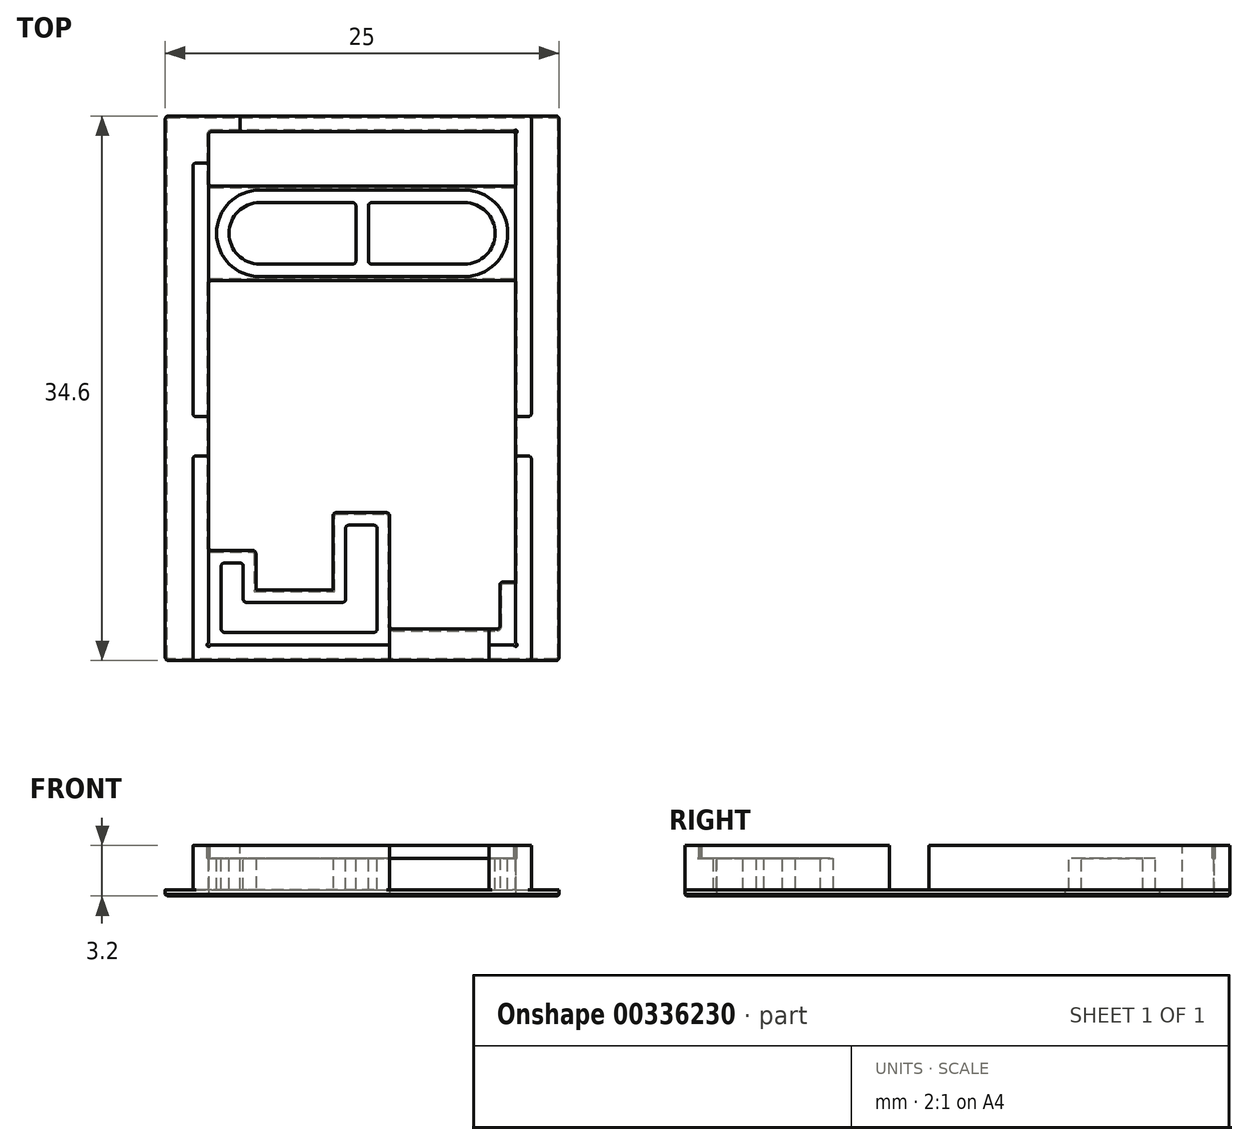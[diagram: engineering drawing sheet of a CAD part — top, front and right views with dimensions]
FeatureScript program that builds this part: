
annotation { "Feature Type Name" : "Feature", "Feature Type Description" : "" }
export const myFeature = defineFeature(function(context is Context, id is Id, definition is map)
    precondition{}
    {
        {
            var Q0;
            Q0=qCreatedBy(makeId("Front.planeOp"),FACE);
            var sketch = newSketch(context, id + "F0", { "sketchPlane" : qUnion([Q0])});
            skLineSegment(sketch, "E0", {"start": v(0, 0) * mm, "end": v(0, 2) * mm});
            skLineSegment(sketch, "E1", {"start": v(0, 0) * mm, "end": v(0, -0.4) * mm});
            skLineSegment(sketch, "E2", {"start": v(0, 2) * mm, "end": v(0, 2.8) * mm});
            skSolve(sketch);
        }
        {
            var Q0;
            Q0=qCreatedBy(makeId("Top.planeOp"),FACE);
            var sketch = newSketch(context, id + "F1", { "sketchPlane" : qUnion([Q0])});
            skLineSegment(sketch, "E3.bottom", {"start": v(9.75, 16.3) * mm, "end": v(-9.75, 16.3) * mm, "construction": true});
            skLineSegment(sketch, "E3.top", {"start": v(9.75, -16.3) * mm, "end": v(-9.75, -16.3) * mm, "construction": true});
            skLineSegment(sketch, "E3.left", {"start": v(9.75, 16.3) * mm, "end": v(9.75, -16.3) * mm, "construction": true});
            skLineSegment(sketch, "E3.right", {"start": v(-9.75, 16.3) * mm, "end": v(-9.75, -16.3) * mm, "construction": true});
            skPoint(sketch, "E3.middle", {"position": v(0, 0) * mm});
            skLineSegment(sketch, "E4", {"start": v(-9.75, 6.3) * mm, "end": v(9.75, 6.3) * mm, "construction": true});
            skLineSegment(sketch, "E5", {"start": v(1.75, -16.3) * mm, "end": v(1.75, -7.9) * mm, "construction": true});
            skLineSegment(sketch, "E6", {"start": v(-1.85, -16.3) * mm, "end": v(-1.85, -7.9) * mm, "construction": true});
            skLineSegment(sketch, "E7", {"start": v(-1.85, -7.9) * mm, "end": v(1.75, -7.9) * mm, "construction": true});
            skLineSegment(sketch, "E8", {"start": v(8.75, -16.3) * mm, "end": v(8.75, -12.3) * mm, "construction": true});
            skLineSegment(sketch, "E9", {"start": v(8.75, -12.3) * mm, "end": v(9.75, -12.3) * mm, "construction": true});
            skLineSegment(sketch, "E10", {"start": v(-9.75, 6.84) * mm, "end": v(9.75, 6.84) * mm, "construction": true});
            skLineSegment(sketch, "E11", {"start": v(-9.75, 12.84) * mm, "end": v(9.75, 12.84) * mm, "construction": true});
            skLineSegment(sketch, "E12", {"start": v(-1.85, -12.8) * mm, "end": v(-9.75, -12.8) * mm, "construction": true});
            skLineSegment(sketch, "E13", {"start": v(-9.75, -10.3) * mm, "end": v(-6.75, -10.3) * mm, "construction": true});
            skLineSegment(sketch, "E14", {"start": v(-6.75, -10.3) * mm, "end": v(-6.75, -12.8) * mm, "construction": true});
            skSolve(sketch);
        }
        {
            var Q0;
            Q0=qCreatedBy(makeId("Top.planeOp"),FACE);
            var sketch = newSketch(context, id + "F2", { "sketchPlane" : qUnion([Q0])});
            skLineSegment(sketch, "E15.bottom", {"start": v(12.5, 17.3) * mm, "end": v(-12.5, 17.3) * mm});
            skLineSegment(sketch, "E15.top", {"start": v(12.5, -17.3) * mm, "end": v(8.75, -17.3) * mm});
            skLineSegment(sketch, "E15.left", {"start": v(12.5, 17.3) * mm, "end": v(12.5, -17.3) * mm});
            skLineSegment(sketch, "E15.right", {"start": v(-12.5, 17.3) * mm, "end": v(-12.5, -17.3) * mm});
            skPoint(sketch, "E15.middle", {"position": v(0, 0) * mm});
            skLineSegment(sketch, "E16.0", {"start": v(9.75, 16.3) * mm, "end": v(-9.75, 16.3) * mm});
            skLineSegment(sketch, "E17.0", {"start": v(-9.75, 12.84) * mm, "end": v(9.75, 12.84) * mm});
            skLineSegment(sketch, "E18", {"start": v(-9.75, 16.3) * mm, "end": v(-9.75, 12.84) * mm});
            skLineSegment(sketch, "E19", {"start": v(9.75, 16.3) * mm, "end": v(9.75, 12.84) * mm});
            skLineSegment(sketch, "E20.0", {"start": v(-9.75, 6.84) * mm, "end": v(9.75, 6.84) * mm});
            skLineSegment(sketch, "E21.0", {"start": v(-9.75, -10.3) * mm, "end": v(-6.75, -10.3) * mm});
            skLineSegment(sketch, "E22.0", {"start": v(-6.75, -10.3) * mm, "end": v(-6.75, -12.8) * mm});
            skLineSegment(sketch, "E23.0", {"start": v(-1.85, -7.9) * mm, "end": v(1.75, -7.9) * mm});
            skLineSegment(sketch, "E24.0", {"start": v(1.75, -16.3) * mm, "end": v(1.75, -7.9) * mm});
            skLineSegment(sketch, "E25.0", {"start": v(8.75, -16.3) * mm, "end": v(8.75, -12.3) * mm});
            skLineSegment(sketch, "E26.0", {"start": v(8.75, -12.3) * mm, "end": v(9.75, -12.3) * mm});
            skLineSegment(sketch, "E27", {"start": v(9.75, 6.84) * mm, "end": v(9.75, -12.3) * mm});
            skLineSegment(sketch, "E28", {"start": v(1.75, -16.3) * mm, "end": v(1.75, -17.3) * mm});
            skLineSegment(sketch, "E29", {"start": v(8.75, -16.3) * mm, "end": v(8.75, -17.3) * mm});
            skLineSegment(sketch, "E30", {"start": v(-6.75, -12.8) * mm, "end": v(-1.85, -12.8) * mm});
            skLineSegment(sketch, "E31", {"start": v(-1.85, -12.8) * mm, "end": v(-1.85, -7.9) * mm});
            skLineSegment(sketch, "E32", {"start": v(-9.75, 6.84) * mm, "end": v(-9.75, -10.3) * mm});
            skLineSegment(sketch, "E33", {"start": v(1.75, -17.3) * mm, "end": v(-12.5, -17.3) * mm});
            skLineSegment(sketch, "E34", {"start": v(8.75, -17.3) * mm, "end": v(1.75, -17.3) * mm});
            skLineSegment(sketch, "E35", {"start": v(1.75, -15.3) * mm, "end": v(8.75, -15.3) * mm});
            skSolve(sketch);
        }
        {
            var Q0;
            Q0 = qSketchRegion(id + "F2", true);
            var Q1;
            Q1=sQuery(id+"F0.wireOp",EDGE,"E1");
            sweep(context, id + "F3", {"profiles" : qUnion([Q0]), "path" : qUnion([Q1])});
        }
        {
            var Q0;
            Q0=makeQuery(id+"F3.opSweep","CAP_FACE",FACE,{"disambiguationData":[OSD([sQuery(id+"F0.wireOp",VERTEX,"E1.start"),sQuery(id+"F2.wireOp",EDGE,"E15.bottom"),sQuery(id+"F2.wireOp",EDGE,"E15.top"),sQuery(id+"F2.wireOp",EDGE,"E15.left"),sQuery(id+"F2.wireOp",EDGE,"E15.right"),sQuery(id+"F2.wireOp",EDGE,"E16.0"),sQuery(id+"F2.wireOp",EDGE,"E17.0"),sQuery(id+"F2.wireOp",EDGE,"E18"),sQuery(id+"F2.wireOp",EDGE,"E19"),sQuery(id+"F2.wireOp",EDGE,"E20.0"),sQuery(id+"F2.wireOp",EDGE,"E21.0"),sQuery(id+"F2.wireOp",EDGE,"E22.0"),sQuery(id+"F2.wireOp",EDGE,"E23.0"),sQuery(id+"F2.wireOp",EDGE,"E24.0"),sQuery(id+"F2.wireOp",EDGE,"E25.0"),sQuery(id+"F2.wireOp",EDGE,"E26.0"),sQuery(id+"F2.wireOp",EDGE,"E27"),sQuery(id+"F2.wireOp",EDGE,"E28"),sQuery(id+"F2.wireOp",EDGE,"E29"),sQuery(id+"F2.wireOp",EDGE,"E30"),sQuery(id+"F2.wireOp",EDGE,"E31"),sQuery(id+"F2.wireOp",EDGE,"E32"),sQuery(id+"F2.wireOp",EDGE,"E33")])],"isStart":true});
            var sketch = newSketch(context, id + "F4", { "sketchPlane" : qUnion([Q0])});
            skPoint(sketch, "E36.0", {"position": v(9.75, -16.3) * mm});
            skLineSegment(sketch, "E37.bottom", {"start": v(8.75, -12.3) * mm, "end": v(9.75, -12.3) * mm});
            skLineSegment(sketch, "E37.top", {"start": v(8.75, -16.3) * mm, "end": v(9.75, -16.3) * mm});
            skLineSegment(sketch, "E37.left", {"start": v(8.75, -12.3) * mm, "end": v(8.75, -15.3) * mm});
            skLineSegment(sketch, "E37.right", {"start": v(9.75, -12.3) * mm, "end": v(9.75, -16.3) * mm});
            skLineSegment(sketch, "E38.0", {"start": v(9.75, -16.3) * mm, "end": v(-9.75, -16.3) * mm, "construction": true});
            skLineSegment(sketch, "E39", {"start": v(1.75, -7.9) * mm, "end": v(1.75, -16.3) * mm});
            skLineSegment(sketch, "E40", {"start": v(1.75, -16.3) * mm, "end": v(-9.75, -16.3) * mm});
            skLineSegment(sketch, "E41", {"start": v(-9.75, -16.3) * mm, "end": v(-9.75, -10.3) * mm});
            skLineSegment(sketch, "E42", {"start": v(-9.75, -10.3) * mm, "end": v(-6.75, -10.3) * mm});
            skLineSegment(sketch, "E43", {"start": v(-6.75, -10.3) * mm, "end": v(-6.75, -12.8) * mm});
            skLineSegment(sketch, "E44", {"start": v(-6.75, -12.8) * mm, "end": v(-1.85, -12.8) * mm});
            skLineSegment(sketch, "E45", {"start": v(-1.85, -12.8) * mm, "end": v(-1.85, -7.9) * mm});
            skLineSegment(sketch, "E46", {"start": v(-1.85, -7.9) * mm, "end": v(1.75, -7.9) * mm});
            skLineSegment(sketch, "E47", {"start": v(0, 12.84) * mm, "end": v(0, 6.84) * mm, "construction": true});
            skLineSegment(sketch, "E48", {"start": v(-6.5, 9.84) * mm, "end": v(6.5, 9.84) * mm, "construction": true});
            skPoint(sketch, "E49", {"position": v(0, 9.84) * mm});
            skArc(sketch, "E50.0.startCap", {"start": v(-6.5, 7.09) * mm, "mid": v(-9.25, 9.84) * mm, "end": v(-6.5, 12.59) * mm});
            skArc(sketch, "E50.0.endCap", {"start": v(6.5, 12.6) * mm, "mid": v(9.25, 9.84) * mm, "end": v(6.5, 7.09) * mm});
            skLineSegment(sketch, "E50.0.left", {"start": v(-6.5, 12.59) * mm, "end": v(6.5, 12.59) * mm});
            skLineSegment(sketch, "E50.0.right", {"start": v(-6.5, 7.09) * mm, "end": v(6.5, 7.1) * mm});
            skArc(sketch, "E51.0", {"start": v(-6.5, 7.89) * mm, "mid": v(-8.45, 9.84) * mm, "end": v(-6.5, 11.79) * mm});
            skLineSegment(sketch, "E51.1", {"start": v(-6.5, 7.89) * mm, "end": v(6.5, 7.89) * mm});
            skArc(sketch, "E51.2", {"start": v(6.5, 11.8) * mm, "mid": v(8.45, 9.84) * mm, "end": v(6.5, 7.89) * mm});
            skLineSegment(sketch, "E51.3", {"start": v(-6.5, 11.79) * mm, "end": v(-0.4, 11.79) * mm});
            skLineSegment(sketch, "E52.0", {"start": v(-8.95, -15.5) * mm, "end": v(-8.95, -11.1) * mm});
            skLineSegment(sketch, "E52.1", {"start": v(0.95, -15.5) * mm, "end": v(-8.95, -15.5) * mm});
            skLineSegment(sketch, "E52.2", {"start": v(-8.95, -11.1) * mm, "end": v(-7.55, -11.1) * mm});
            skLineSegment(sketch, "E52.3", {"start": v(0.95, -8.7) * mm, "end": v(0.95, -15.5) * mm});
            skLineSegment(sketch, "E52.4", {"start": v(-7.55, -11.1) * mm, "end": v(-7.55, -13.6) * mm});
            skLineSegment(sketch, "E52.5", {"start": v(-7.55, -13.6) * mm, "end": v(-1.05, -13.6) * mm});
            skLineSegment(sketch, "E52.6", {"start": v(-1.05, -13.6) * mm, "end": v(-1.05, -8.7) * mm});
            skLineSegment(sketch, "E52.7", {"start": v(-1.05, -8.7) * mm, "end": v(0.95, -8.7) * mm});
            skLineSegment(sketch, "E53", {"start": v(-0.4, 11.79) * mm, "end": v(-0.4, 7.9) * mm});
            skLineSegment(sketch, "E54", {"start": v(0.4, 11.79) * mm, "end": v(0.4, 7.9) * mm});
            skLineSegment(sketch, "E55", {"start": v(-0.4, 11.79) * mm, "end": v(0.4, 11.79) * mm, "construction": true});
            skLineSegment(sketch, "E56", {"start": v(-0.4, 11.79) * mm, "end": v(-0.4, 11.79) * mm});
            skLineSegment(sketch, "E57", {"start": v(0.4, 11.79) * mm, "end": v(6.5, 11.8) * mm});
            skLineSegment(sketch, "E58", {"start": v(8.75, -16.3) * mm, "end": v(8.05, -16.3) * mm});
            skLineSegment(sketch, "E59", {"start": v(8.05, -16.3) * mm, "end": v(8.05, -15.3) * mm});
            skLineSegment(sketch, "E60", {"start": v(8.05, -15.3) * mm, "end": v(8.75, -15.3) * mm});
            skLineSegment(sketch, "E61", {"start": v(8.75, -15.3) * mm, "end": v(8.75, -16.3) * mm, "construction": true});
            skSolve(sketch);
        }
        {
            var Q0;
            Q0 = qSketchRegion(id + "F4", true);
            var Q1;
            Q1=sQuery(id+"F0.wireOp",EDGE,"E0");
            sweep(context, id + "F5", {"operationType" : NewBodyOperationType.ADD, "profiles" : qUnion([Q0]), "path" : qUnion([Q1])});
        }
        {
            var Q0;
            Q0=qCreatedBy(makeId("Top.planeOp"),FACE);
            var sketch = newSketch(context, id + "F6", { "sketchPlane" : qUnion([Q0])});
            skLineSegment(sketch, "E62.0", {"start": v(8.05, -16.3) * mm, "end": v(9.75, -16.3) * mm});
            skLineSegment(sketch, "E63", {"start": v(8.75, -17.3) * mm, "end": v(10.75, -17.3) * mm});
            skLineSegment(sketch, "E64.0", {"start": v(9.75, 16.3) * mm, "end": v(-9.75, 16.3) * mm, "construction": true});
            skLineSegment(sketch, "E65.0", {"start": v(12.5, 17.3) * mm, "end": v(-12.5, 17.3) * mm, "construction": true});
            skLineSegment(sketch, "E66.0", {"start": v(1.75, -16.3) * mm, "end": v(1.75, -17.3) * mm});
            skLineSegment(sketch, "E67", {"start": v(-9.75, -16.3) * mm, "end": v(1.75, -16.3) * mm});
            skLineSegment(sketch, "E68", {"start": v(9.75, 16.3) * mm, "end": v(9.75, -16.3) * mm});
            skLineSegment(sketch, "E69", {"start": v(10.75, 17.3) * mm, "end": v(10.75, -1.8) * mm});
            skLineSegment(sketch, "E70", {"start": v(-7.75, 16.3) * mm, "end": v(9.75, 16.3) * mm});
            skLineSegment(sketch, "E71", {"start": v(-7.75, 16.3) * mm, "end": v(-7.75, 17.3) * mm});
            skLineSegment(sketch, "E72", {"start": v(-7.75, 17.3) * mm, "end": v(10.75, 17.3) * mm});
            skLineSegment(sketch, "E73", {"start": v(-9.75, 14.3) * mm, "end": v(-9.75, -16.3) * mm});
            skLineSegment(sketch, "E74", {"start": v(-9.75, 14.3) * mm, "end": v(-10.75, 14.3) * mm});
            skLineSegment(sketch, "E75", {"start": v(-10.75, 14.3) * mm, "end": v(-10.75, -1.8) * mm});
            skLineSegment(sketch, "E76", {"start": v(-10.75, -17.3) * mm, "end": v(1.75, -17.3) * mm});
            skLineSegment(sketch, "E77", {"start": v(-10.75, -1.8) * mm, "end": v(-9.75, -1.8) * mm});
            skLineSegment(sketch, "E78", {"start": v(-10.75, -4.3) * mm, "end": v(-9.75, -4.3) * mm});
            skLineSegment(sketch, "E79", {"start": v(9.75, -1.8) * mm, "end": v(10.75, -1.8) * mm});
            skLineSegment(sketch, "E80", {"start": v(9.75, -4.3) * mm, "end": v(10.75, -4.3) * mm});
            skLineSegment(sketch, "E81", {"start": v(-10.75, -1.8) * mm, "end": v(-10.75, -4.3) * mm, "construction": true});
            skLineSegment(sketch, "E82", {"start": v(-10.75, -4.3) * mm, "end": v(-10.75, -17.3) * mm});
            skLineSegment(sketch, "E83", {"start": v(10.75, -1.8) * mm, "end": v(10.75, -4.3) * mm, "construction": true});
            skLineSegment(sketch, "E84", {"start": v(10.75, -4.3) * mm, "end": v(10.75, -17.3) * mm});
            skLineSegment(sketch, "E85", {"start": v(8.05, -16.3) * mm, "end": v(8.05, -17.3) * mm});
            skLineSegment(sketch, "E86", {"start": v(8.05, -17.3) * mm, "end": v(8.75, -17.3) * mm});
            skSolve(sketch);
        }
        {
            var Q0;
            Q0 = qSketchRegion(id + "F6", true);
            var Q1;
            Q1=sQuery(id+"F0.wireOp",EDGE,"E0");
            var Q2;
            Q2=sQuery(id+"F0.wireOp",EDGE,"E2");
            sweep(context, id + "F7", {"operationType" : NewBodyOperationType.ADD, "profiles" : qUnion([Q0]), "path" : qUnion([Q1, Q2])});
        }
        {
            var Q0;
            Q0=makeQuery(id+"F7.opSweep","CAP_FACE",FACE,{"disambiguationData":[OSD([sQuery(id+"F0.wireOp",VERTEX,"E2.end"),sQuery(id+"F6.wireOp",EDGE,"E62.0"),sQuery(id+"F6.wireOp",EDGE,"640f83d2-e44f-404a-a3b5-877292df678b.0"),sQuery(id+"F6.wireOp",EDGE,"E63"),sQuery(id+"F6.wireOp",EDGE,"E68"),sQuery(id+"F6.wireOp",EDGE,"E69"),sQuery(id+"F6.wireOp",EDGE,"E70"),sQuery(id+"F6.wireOp",EDGE,"E71"),sQuery(id+"F6.wireOp",EDGE,"E72")])],"isStart":false});
            var sketch = newSketch(context, id + "F8", { "sketchPlane" : qUnion([Q0])});
            skCircle(sketch, "E87", {"center": v(9.75, 16.3) * mm, "radius": 0.1 * mm});
            skPoint(sketch, "E88.0", {"position": v(-9.75, -16.3) * mm});
            skCircle(sketch, "E89", {"center": v(-9.75, -16.3) * mm, "radius": 0.1 * mm});
            skCircle(sketch, "E90", {"center": v(9.75, -16.3) * mm, "radius": 0.1 * mm});
            skSolve(sketch);
        }
        {
            var Q0;
            Q0 = qSketchRegion(id + "F8", true);
            var Q1;
            Q1=makeQuery(id+"F5.opSweep","CAP_FACE",FACE,{"disambiguationData":[OSD([sQuery(id+"F0.wireOp",VERTEX,"E0.end"),sQuery(id+"F4.wireOp",EDGE,"E39"),sQuery(id+"F4.wireOp",EDGE,"E40"),sQuery(id+"F4.wireOp",EDGE,"E41"),sQuery(id+"F4.wireOp",EDGE,"E42"),sQuery(id+"F4.wireOp",EDGE,"E43"),sQuery(id+"F4.wireOp",EDGE,"E44"),sQuery(id+"F4.wireOp",EDGE,"E45"),sQuery(id+"F4.wireOp",EDGE,"E46"),sQuery(id+"F4.wireOp",EDGE,"E52.0"),sQuery(id+"F4.wireOp",EDGE,"E52.1"),sQuery(id+"F4.wireOp",EDGE,"E52.2"),sQuery(id+"F4.wireOp",EDGE,"E52.3"),sQuery(id+"F4.wireOp",EDGE,"E52.4"),sQuery(id+"F4.wireOp",EDGE,"E52.5"),sQuery(id+"F4.wireOp",EDGE,"E52.6"),sQuery(id+"F4.wireOp",EDGE,"E52.7")])],"isStart":false});
            extrude(context, id + "F9", {"entities" : qUnion([Q0]), "operationType" : NewBodyOperationType.REMOVE, "endBound" : BoundingType.UP_TO_SURFACE, "oppositeDirection" : true, "endBoundEntityFace" : qUnion([Q1]), "depth" : 25 * mm});
        }
        {
            var Q0;
            Q0=makeQuery(id+"F3.opSweep","SWEPT_EDGE",EDGE,{"disambiguationData":[OSD([sQuery(id+"F0.wireOp",EDGE,"E1"),sQuery(id+"F2.wireOp",EDGE,"E24.0"),sQuery(id+"F2.wireOp",EDGE,"E35")])]});
            var Q1;
            Q1=makeQuery(id+"F3.opSweep","SWEPT_EDGE",EDGE,{"disambiguationData":[OSD([sQuery(id+"F0.wireOp",EDGE,"E1"),sQuery(id+"F2.wireOp",EDGE,"E25.0"),sQuery(id+"F2.wireOp",EDGE,"E35")])]});
            var Q2;
            Q2=makeQuery(id+"F5.opSweep","SWEPT_EDGE",EDGE,{"disambiguationData":[OSD([sQuery(id+"F0.wireOp",EDGE,"E0"),sQuery(id+"F4.wireOp",EDGE,"E54"),sQuery(id+"F4.wireOp",EDGE,"E57")])]});
            var Q3;
            Q3=makeQuery(id+"F5.opSweep","SWEPT_EDGE",EDGE,{"disambiguationData":[OSD([sQuery(id+"F0.wireOp",EDGE,"E0"),sQuery(id+"F4.wireOp",EDGE,"E51.3"),sQuery(id+"F4.wireOp",EDGE,"E53")])]});
            var Q4;
            Q4=makeQuery(id+"F5.opSweep","SWEPT_EDGE",EDGE,{"disambiguationData":[OSD([sQuery(id+"F0.wireOp",EDGE,"E0"),sQuery(id+"F4.wireOp",EDGE,"E51.1"),sQuery(id+"F4.wireOp",EDGE,"E53")])]});
            var Q5;
            Q5=makeQuery(id+"F5.opSweep","SWEPT_EDGE",EDGE,{"disambiguationData":[OSD([sQuery(id+"F0.wireOp",EDGE,"E0"),sQuery(id+"F4.wireOp",EDGE,"E51.1"),sQuery(id+"F4.wireOp",EDGE,"E54")])]});
            var Q6;
            Q6=makeQuery(id+"F7.opSweep","SWEPT_EDGE",EDGE,{"disambiguationData":[OSD([sQuery(id+"F0.wireOp",EDGE,"E0"),sQuery(id+"F6.wireOp",EDGE,"E68"),sQuery(id+"F6.wireOp",EDGE,"E79")])]});
            var Q7;
            Q7=makeQuery(id+"F7.opSweep","SWEPT_EDGE",EDGE,{"disambiguationData":[OSD([sQuery(id+"F0.wireOp",EDGE,"E0"),sQuery(id+"F6.wireOp",EDGE,"E69"),sQuery(id+"F6.wireOp",EDGE,"E79")])]});
            var Q8;
            Q8=makeQuery(id+"F7.opSweep","SWEPT_EDGE",EDGE,{"disambiguationData":[OSD([sQuery(id+"F0.wireOp",EDGE,"E0"),sQuery(id+"F6.wireOp",EDGE,"E63"),sQuery(id+"F6.wireOp",EDGE,"E84")])]});
            var Q9;
            Q9=makeQuery(id+"F3.opSweep","SWEPT_EDGE",EDGE,{"disambiguationData":[OSD([sQuery(id+"F0.wireOp",EDGE,"E1"),sQuery(id+"F2.wireOp",EDGE,"E15.top"),sQuery(id+"F2.wireOp",EDGE,"E15.left")])]});
            var Q10;
            Q10=makeQuery(id+"F5.boolean.opBoolean","MERGE",EDGE,{"derivedFrom":[makeQuery(id+"F3.opSweep","SWEPT_EDGE",EDGE,{"disambiguationData":[OSD([sQuery(id+"F0.wireOp",EDGE,"E1"),sQuery(id+"F2.wireOp",EDGE,"E25.0"),sQuery(id+"F2.wireOp",EDGE,"E26.0")])]}),makeQuery(id+"F5.opSweep","SWEPT_EDGE",EDGE,{"disambiguationData":[OSD([sQuery(id+"F0.wireOp",EDGE,"E0"),sQuery(id+"F4.wireOp",EDGE,"E37.bottom"),sQuery(id+"F4.wireOp",EDGE,"E37.left")])]})]});
            var Q11;
            Q11=makeQuery(id+"F7.opSweep","SWEPT_EDGE",EDGE,{"disambiguationData":[OSD([sQuery(id+"F0.wireOp",EDGE,"E0"),sQuery(id+"F6.wireOp",EDGE,"640f83d2-e44f-404a-a3b5-877292df678b.0"),sQuery(id+"F6.wireOp",EDGE,"E63")])]});
            var Q12;
            Q12=makeQuery(id+"F7.opSweep","SWEPT_EDGE",EDGE,{"disambiguationData":[OSD([sQuery(id+"F0.wireOp",EDGE,"E0"),sQuery(id+"F6.wireOp",EDGE,"E66.0"),sQuery(id+"F6.wireOp",EDGE,"E76")])]});
            var Q13;
            Q13=makeQuery(id+"F5.boolean.opBoolean","MERGE",EDGE,{"derivedFrom":[makeQuery(id+"F3.opSweep","SWEPT_EDGE",EDGE,{"disambiguationData":[OSD([sQuery(id+"F0.wireOp",EDGE,"E1"),sQuery(id+"F2.wireOp",EDGE,"E23.0"),sQuery(id+"F2.wireOp",EDGE,"E31")])]}),makeQuery(id+"F5.opSweep","SWEPT_EDGE",EDGE,{"disambiguationData":[OSD([sQuery(id+"F0.wireOp",EDGE,"E0"),sQuery(id+"F4.wireOp",EDGE,"E45"),sQuery(id+"F4.wireOp",EDGE,"E46")])]})]});
            var Q14;
            Q14=makeQuery(id+"F3.opSweep","SWEPT_EDGE",EDGE,{"disambiguationData":[OSD([sQuery(id+"F0.wireOp",EDGE,"E1"),sQuery(id+"F2.wireOp",EDGE,"E20.0"),sQuery(id+"F2.wireOp",EDGE,"E27")])]});
            var Q15;
            Q15=makeQuery(id+"F7.boolean.opBoolean","MERGE",EDGE,{"derivedFrom":[makeQuery(id+"F3.opSweep","SWEPT_EDGE",EDGE,{"disambiguationData":[OSD([sQuery(id+"F0.wireOp",EDGE,"E1"),sQuery(id+"F2.wireOp",EDGE,"E16.0"),sQuery(id+"F2.wireOp",EDGE,"E19")])]}),makeQuery(id+"F7.opSweep","SWEPT_EDGE",EDGE,{"disambiguationData":[OSD([sQuery(id+"F0.wireOp",EDGE,"E0"),sQuery(id+"F6.wireOp",EDGE,"E68"),sQuery(id+"F6.wireOp",EDGE,"E70")])]})]});
            var Q16;
            Q16=makeQuery(id+"F7.opSweep","SWEPT_EDGE",EDGE,{"disambiguationData":[OSD([sQuery(id+"F0.wireOp",EDGE,"E0"),sQuery(id+"F6.wireOp",EDGE,"E78"),sQuery(id+"F6.wireOp",EDGE,"E82")])]});
            var Q17;
            Q17=makeQuery(id+"F7.opSweep","SWEPT_EDGE",EDGE,{"disambiguationData":[OSD([sQuery(id+"F0.wireOp",EDGE,"E0"),sQuery(id+"F6.wireOp",EDGE,"E75"),sQuery(id+"F6.wireOp",EDGE,"E77")])]});
            var Q18;
            Q18=makeQuery(id+"F7.opSweep","SWEPT_EDGE",EDGE,{"disambiguationData":[OSD([sQuery(id+"F0.wireOp",EDGE,"E0"),sQuery(id+"F6.wireOp",EDGE,"E73"),sQuery(id+"F6.wireOp",EDGE,"E77")])]});
            var Q19;
            Q19=makeQuery(id+"F7.opSweep","SWEPT_EDGE",EDGE,{"disambiguationData":[OSD([sQuery(id+"F0.wireOp",EDGE,"E0"),sQuery(id+"F6.wireOp",EDGE,"E76"),sQuery(id+"F6.wireOp",EDGE,"E82")])]});
            var Q20;
            Q20=makeQuery(id+"F3.opSweep","SWEPT_EDGE",EDGE,{"disambiguationData":[OSD([sQuery(id+"F0.wireOp",EDGE,"E1"),sQuery(id+"F2.wireOp",EDGE,"E15.right"),sQuery(id+"F2.wireOp",EDGE,"E33")])]});
            var Q21;
            Q21=makeQuery(id+"F3.opSweep","SWEPT_EDGE",EDGE,{"disambiguationData":[OSD([sQuery(id+"F0.wireOp",EDGE,"E1"),sQuery(id+"F2.wireOp",EDGE,"E15.bottom"),sQuery(id+"F2.wireOp",EDGE,"E15.right")])]});
            var Q22;
            Q22=makeQuery(id+"F7.opSweep","SWEPT_EDGE",EDGE,{"disambiguationData":[OSD([sQuery(id+"F0.wireOp",EDGE,"E0"),sQuery(id+"F6.wireOp",EDGE,"E74"),sQuery(id+"F6.wireOp",EDGE,"E75")])]});
            var Q23;
            Q23=makeQuery(id+"F7.opSweep","SWEPT_EDGE",EDGE,{"disambiguationData":[OSD([sQuery(id+"F0.wireOp",EDGE,"E0"),sQuery(id+"F6.wireOp",EDGE,"E71"),sQuery(id+"F6.wireOp",EDGE,"E72")])]});
            var Q24;
            Q24=makeQuery(id+"F7.opSweep","SWEPT_EDGE",EDGE,{"disambiguationData":[OSD([sQuery(id+"F0.wireOp",EDGE,"E0"),sQuery(id+"F6.wireOp",EDGE,"E70"),sQuery(id+"F6.wireOp",EDGE,"E71")])]});
            var Q25;
            Q25=makeQuery(id+"F3.opSweep","SWEPT_EDGE",EDGE,{"disambiguationData":[OSD([sQuery(id+"F0.wireOp",EDGE,"E1"),sQuery(id+"F2.wireOp",EDGE,"E16.0"),sQuery(id+"F2.wireOp",EDGE,"E18")])]});
            var Q26;
            Q26=makeQuery(id+"F7.opSweep","SWEPT_EDGE",EDGE,{"disambiguationData":[OSD([sQuery(id+"F0.wireOp",EDGE,"E0"),sQuery(id+"F6.wireOp",EDGE,"E69"),sQuery(id+"F6.wireOp",EDGE,"E72")])]});
            var Q27;
            Q27=makeQuery(id+"F3.opSweep","SWEPT_EDGE",EDGE,{"disambiguationData":[OSD([sQuery(id+"F0.wireOp",EDGE,"E1"),sQuery(id+"F2.wireOp",EDGE,"E15.bottom"),sQuery(id+"F2.wireOp",EDGE,"E15.left")])]});
            var Q28;
            Q28=makeQuery(id+"F7.opSweep","SWEPT_EDGE",EDGE,{"disambiguationData":[OSD([sQuery(id+"F0.wireOp",EDGE,"E0"),sQuery(id+"F6.wireOp",EDGE,"E68"),sQuery(id+"F6.wireOp",EDGE,"E80")])]});
            var Q29;
            Q29=makeQuery(id+"F5.boolean.opBoolean","MERGE",EDGE,{"derivedFrom":[makeQuery(id+"F3.opSweep","SWEPT_EDGE",EDGE,{"disambiguationData":[OSD([sQuery(id+"F0.wireOp",EDGE,"E1"),sQuery(id+"F2.wireOp",EDGE,"E23.0"),sQuery(id+"F2.wireOp",EDGE,"E24.0")])]}),makeQuery(id+"F5.opSweep","SWEPT_EDGE",EDGE,{"disambiguationData":[OSD([sQuery(id+"F0.wireOp",EDGE,"E0"),sQuery(id+"F4.wireOp",EDGE,"E39"),sQuery(id+"F4.wireOp",EDGE,"E46")])]})]});
            var Q30;
            Q30=makeQuery(id+"F5.opSweep","SWEPT_EDGE",EDGE,{"disambiguationData":[OSD([sQuery(id+"F0.wireOp",EDGE,"E0"),sQuery(id+"F4.wireOp",EDGE,"E52.3"),sQuery(id+"F4.wireOp",EDGE,"E52.7")])]});
            var Q31;
            Q31=makeQuery(id+"F5.opSweep","SWEPT_EDGE",EDGE,{"disambiguationData":[OSD([sQuery(id+"F0.wireOp",EDGE,"E0"),sQuery(id+"F4.wireOp",EDGE,"E52.6"),sQuery(id+"F4.wireOp",EDGE,"E52.7")])]});
            var Q32;
            Q32=makeQuery(id+"F5.opSweep","SWEPT_EDGE",EDGE,{"disambiguationData":[OSD([sQuery(id+"F0.wireOp",EDGE,"E0"),sQuery(id+"F4.wireOp",EDGE,"E52.0"),sQuery(id+"F4.wireOp",EDGE,"E52.2")])]});
            var Q33;
            Q33=makeQuery(id+"F5.opSweep","SWEPT_EDGE",EDGE,{"disambiguationData":[OSD([sQuery(id+"F0.wireOp",EDGE,"E0"),sQuery(id+"F4.wireOp",EDGE,"E52.2"),sQuery(id+"F4.wireOp",EDGE,"E52.4")])]});
            var Q34;
            Q34=makeQuery(id+"F5.opSweep","SWEPT_EDGE",EDGE,{"disambiguationData":[OSD([sQuery(id+"F0.wireOp",EDGE,"E0"),sQuery(id+"F4.wireOp",EDGE,"E52.4"),sQuery(id+"F4.wireOp",EDGE,"E52.5")])]});
            var Q35;
            Q35=makeQuery(id+"F5.opSweep","SWEPT_EDGE",EDGE,{"disambiguationData":[OSD([sQuery(id+"F0.wireOp",EDGE,"E0"),sQuery(id+"F4.wireOp",EDGE,"E52.5"),sQuery(id+"F4.wireOp",EDGE,"E52.6")])]});
            var Q36;
            Q36=makeQuery(id+"F5.opSweep","SWEPT_EDGE",EDGE,{"disambiguationData":[OSD([sQuery(id+"F0.wireOp",EDGE,"E0"),sQuery(id+"F4.wireOp",EDGE,"E52.1"),sQuery(id+"F4.wireOp",EDGE,"E52.3")])]});
            var Q37;
            Q37=makeQuery(id+"F5.opSweep","SWEPT_EDGE",EDGE,{"disambiguationData":[OSD([sQuery(id+"F0.wireOp",EDGE,"E0"),sQuery(id+"F4.wireOp",EDGE,"E52.0"),sQuery(id+"F4.wireOp",EDGE,"E52.1")])]});
            var Q38;
            Q38=makeQuery(id+"F7.opSweep","SWEPT_EDGE",EDGE,{"disambiguationData":[OSD([sQuery(id+"F0.wireOp",EDGE,"E0"),sQuery(id+"F6.wireOp",EDGE,"E73"),sQuery(id+"F6.wireOp",EDGE,"E78")])]});
            var Q39;
            Q39=makeQuery(id+"F3.opSweep","SWEPT_EDGE",EDGE,{"disambiguationData":[OSD([sQuery(id+"F0.wireOp",EDGE,"E1"),sQuery(id+"F2.wireOp",EDGE,"E20.0"),sQuery(id+"F2.wireOp",EDGE,"E32")])]});
            var Q40;
            Q40=makeQuery(id+"F7.opSweep","SWEPT_EDGE",EDGE,{"disambiguationData":[OSD([sQuery(id+"F0.wireOp",EDGE,"E0"),sQuery(id+"F6.wireOp",EDGE,"E73"),sQuery(id+"F6.wireOp",EDGE,"E74")])]});
            var Q41;
            Q41=makeQuery(id+"F7.opSweep","SWEPT_EDGE",EDGE,{"disambiguationData":[OSD([sQuery(id+"F0.wireOp",EDGE,"E0"),sQuery(id+"F6.wireOp",EDGE,"E80"),sQuery(id+"F6.wireOp",EDGE,"E84")])]});
            var Q42;
            Q42=makeQuery(id+"F5.boolean.opBoolean","MERGE",EDGE,{"derivedFrom":[makeQuery(id+"F3.opSweep","SWEPT_EDGE",EDGE,{"disambiguationData":[OSD([sQuery(id+"F0.wireOp",EDGE,"E1"),sQuery(id+"F2.wireOp",EDGE,"E21.0"),sQuery(id+"F2.wireOp",EDGE,"E22.0")])]}),makeQuery(id+"F5.opSweep","SWEPT_EDGE",EDGE,{"disambiguationData":[OSD([sQuery(id+"F0.wireOp",EDGE,"E0"),sQuery(id+"F4.wireOp",EDGE,"E42"),sQuery(id+"F4.wireOp",EDGE,"E43")])]})]});
            var Q43;
            {var subQ0=sQuery(id+"F2.wireOp",EDGE,"E32");Q43=makeQuery(id+"F7.boolean.opBoolean","MERGE",EDGE,{"derivedFrom":[makeQuery(id+"F3.opSweep","SWEPT_EDGE",EDGE,{"disambiguationData":[OSD([sQuery(id+"F0.wireOp",EDGE,"E1"),sQuery(id+"F2.wireOp",EDGE,"E21.0"),subQ0])]}),makeQuery(id+"F5.opSweep","SWEPT_EDGE",EDGE,{"disambiguationData":[OSD([sQuery(id+"F0.wireOp",VERTEX,"E1.start"),sQuery(id+"F0.wireOp",EDGE,"E0"),subQ0,sQuery(id+"F4.wireOp",EDGE,"E41"),sQuery(id+"F4.wireOp",EDGE,"E42")])]})]});}
            var Q44;
            Q44=makeQuery(id+"F7.opSweep","SWEPT_EDGE",EDGE,{"disambiguationData":[OSD([sQuery(id+"F0.wireOp",EDGE,"E0"),sQuery(id+"F6.wireOp",EDGE,"E66.0"),sQuery(id+"F6.wireOp",EDGE,"E67")])]});
            var Q45;
            Q45=makeQuery(id+"F3.opSweep","SWEPT_EDGE",EDGE,{"disambiguationData":[OSD([sQuery(id+"F0.wireOp",EDGE,"E1"),sQuery(id+"F2.wireOp",EDGE,"E17.0"),sQuery(id+"F2.wireOp",EDGE,"E19")])]});
            var Q46;
            Q46=makeQuery(id+"F3.opSweep","SWEPT_EDGE",EDGE,{"disambiguationData":[OSD([sQuery(id+"F0.wireOp",EDGE,"E1"),sQuery(id+"F2.wireOp",EDGE,"E17.0"),sQuery(id+"F2.wireOp",EDGE,"E18")])]});
            var Q47;
            Q47=makeQuery(id+"F5.opSweep","SWEPT_EDGE",EDGE,{"disambiguationData":[OSD([sQuery(id+"F0.wireOp",VERTEX,"E1.start"),sQuery(id+"F0.wireOp",EDGE,"E0"),sQuery(id+"F2.wireOp",EDGE,"E35"),sQuery(id+"F4.wireOp",EDGE,"E59"),sQuery(id+"F4.wireOp",EDGE,"E60")])]});
            var Q48;
            Q48=makeQuery(id+"F7.opSweep","SWEPT_EDGE",EDGE,{"disambiguationData":[OSD([sQuery(id+"F0.wireOp",EDGE,"E0"),sQuery(id+"F6.wireOp",EDGE,"E62.0"),sQuery(id+"F6.wireOp",EDGE,"E85")])]});
            var Q49;
            Q49=makeQuery(id+"F7.opSweep","SWEPT_EDGE",EDGE,{"disambiguationData":[OSD([sQuery(id+"F0.wireOp",EDGE,"E0"),sQuery(id+"F6.wireOp",EDGE,"E85"),sQuery(id+"F6.wireOp",EDGE,"E86")])]});
            fillet(context, id + "F10", {"entities" : qUnion([Q0, Q1, Q2, Q3, Q4, Q5, Q6, Q7, Q8, Q9, Q10, Q11, Q12, Q13, Q14, Q15, Q16, Q17, Q18, Q19, Q20, Q21, Q22, Q23, Q24, Q25, Q26, Q27, Q28, Q29, Q30, Q31, Q32, Q33, Q34, Q35, Q36, Q37, Q38, Q39, Q40, Q41, Q42, Q43, Q44, Q45, Q46, Q47, Q48, Q49]), "radius" : 0.2 * mm, "allowEdgeOverflow" : false});
        }
        {
            var Q0;
            Q0=makeQuery(id+"F3.opSweep","CAP_FACE",FACE,{"disambiguationData":[OSD([sQuery(id+"F0.wireOp",VERTEX,"E1.end"),sQuery(id+"F2.wireOp",EDGE,"E15.bottom"),sQuery(id+"F2.wireOp",EDGE,"E15.top"),sQuery(id+"F2.wireOp",EDGE,"E15.left"),sQuery(id+"F2.wireOp",EDGE,"E15.right"),sQuery(id+"F2.wireOp",EDGE,"E16.0"),sQuery(id+"F2.wireOp",EDGE,"E17.0"),sQuery(id+"F2.wireOp",EDGE,"E18"),sQuery(id+"F2.wireOp",EDGE,"E19"),sQuery(id+"F2.wireOp",EDGE,"E20.0"),sQuery(id+"F2.wireOp",EDGE,"E21.0"),sQuery(id+"F2.wireOp",EDGE,"E22.0"),sQuery(id+"F2.wireOp",EDGE,"E23.0"),sQuery(id+"F2.wireOp",EDGE,"E24.0"),sQuery(id+"F2.wireOp",EDGE,"E25.0"),sQuery(id+"F2.wireOp",EDGE,"E26.0"),sQuery(id+"F2.wireOp",EDGE,"E27"),sQuery(id+"F2.wireOp",EDGE,"E30"),sQuery(id+"F2.wireOp",EDGE,"E31"),sQuery(id+"F2.wireOp",EDGE,"E32"),sQuery(id+"F2.wireOp",EDGE,"E33"),sQuery(id+"F2.wireOp",EDGE,"E34"),sQuery(id+"F2.wireOp",EDGE,"E35")])],"isStart":false});
            chamfer(context, id + "F11", {"entities" : qUnion([Q0]), "width" : 0.1 * mm});
        }
    });
